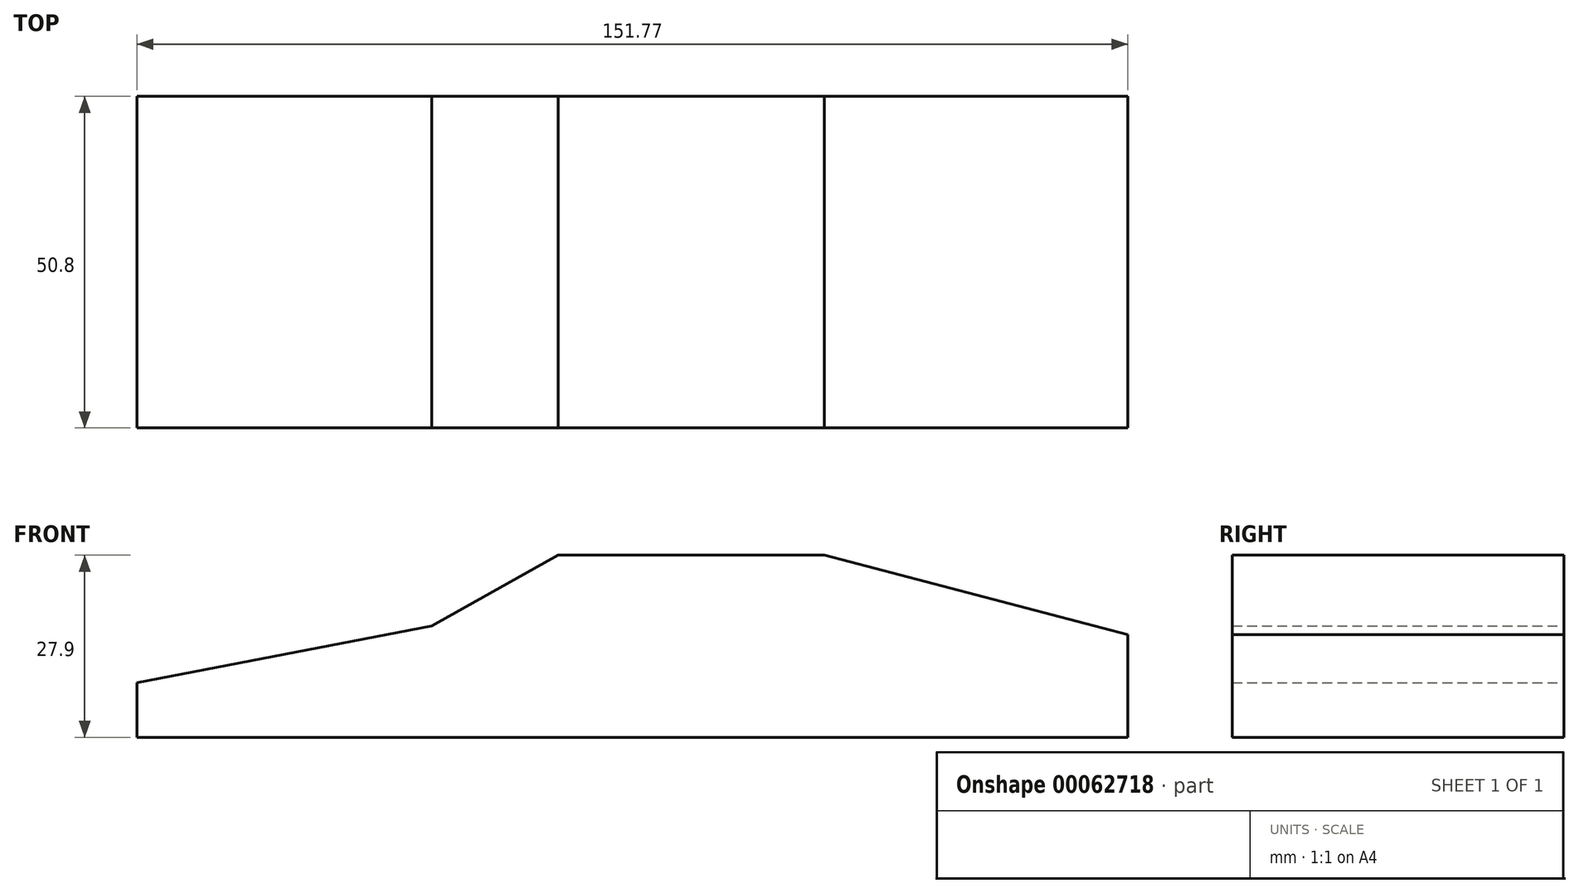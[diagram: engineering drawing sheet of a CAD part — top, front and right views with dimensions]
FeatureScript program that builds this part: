
annotation { "Feature Type Name" : "Feature", "Feature Type Description" : "" }
export const myFeature = defineFeature(function(context is Context, id is Id, definition is map)
    precondition{}
    {
        {
            var Q0;
            Q0=qCreatedBy(makeId("Front.planeOp"),FACE);
            var sketch = newSketch(context, id + "F0", { "sketchPlane" : qUnion([Q0])});
            skLineSegment(sketch, "E0", {"start": v(-66.33, 0) * mm, "end": v(-66.33, 8.36) * mm});
            skLineSegment(sketch, "E1", {"start": v(-66.33, 8.36) * mm, "end": v(-21.17, 17.04) * mm});
            skLineSegment(sketch, "E2", {"start": v(-21.17, 17.04) * mm, "end": v(-1.85, 27.9) * mm});
            skLineSegment(sketch, "E3", {"start": v(-1.85, 27.9) * mm, "end": v(38.97, 27.9) * mm});
            skLineSegment(sketch, "E4", {"start": v(38.97, 27.9) * mm, "end": v(85.44, 15.74) * mm});
            skLineSegment(sketch, "E5", {"start": v(85.44, 15.74) * mm, "end": v(85.44, 0) * mm});
            skLineSegment(sketch, "E6", {"start": v(85.44, 0) * mm, "end": v(-66.33, 0) * mm});
            skSolve(sketch);
        }
        {
            var Q0;
            Q0 = qSketchRegion(id + "F0", true);
            extrude(context, id + "F1", {"entities" : qUnion([Q0]), "depth" : 25.4 * mm, "hasSecondDirection" : true, "secondDirectionOppositeDirection" : true, "secondDirectionDepth" : 25.4 * mm});
        }
    });
